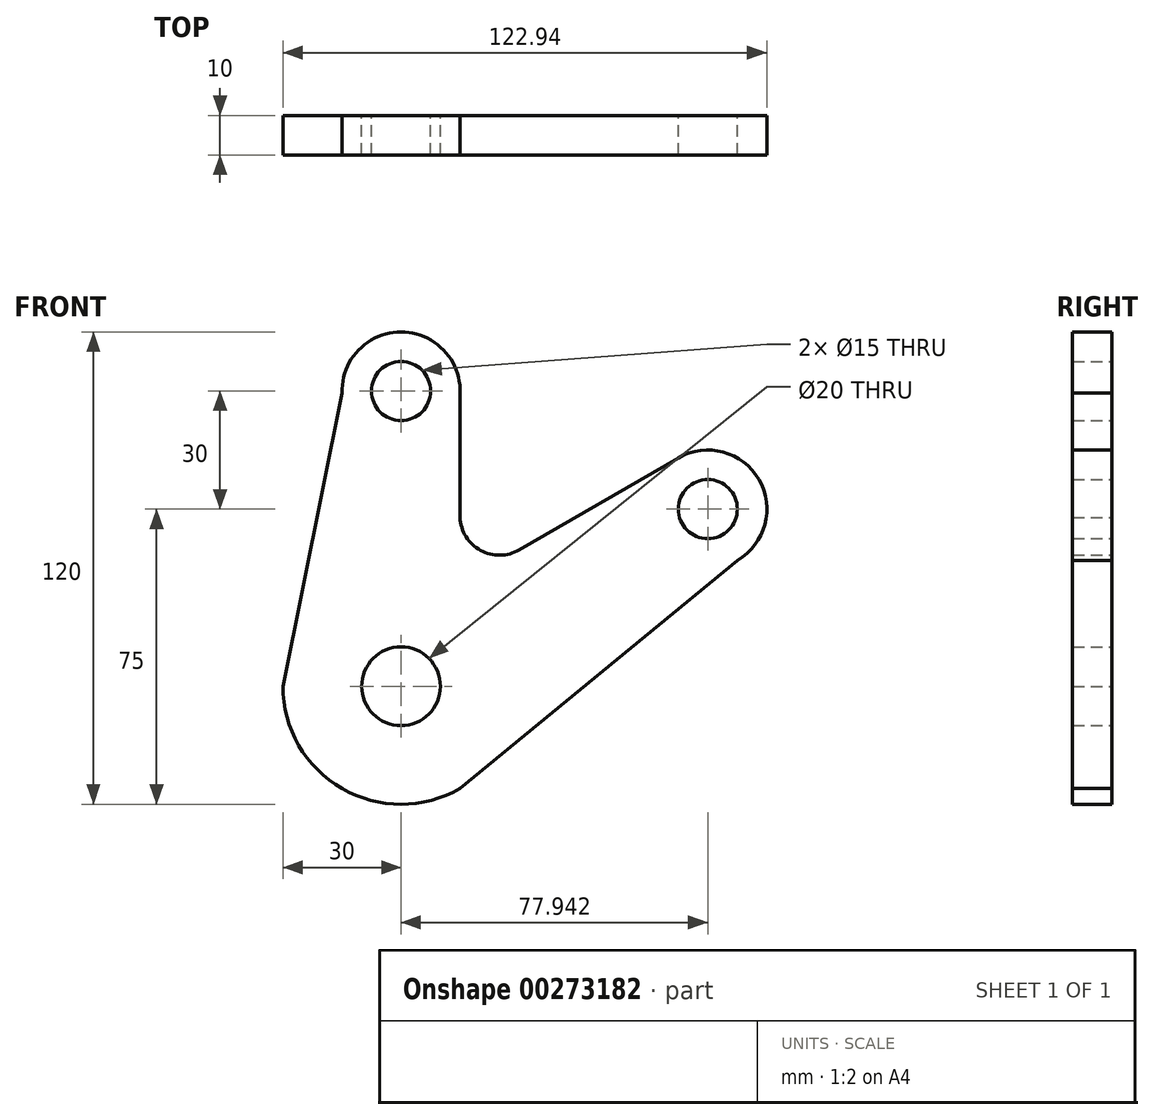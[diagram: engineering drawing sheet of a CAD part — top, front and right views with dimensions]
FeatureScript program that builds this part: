
annotation { "Feature Type Name" : "Feature", "Feature Type Description" : "" }
export const myFeature = defineFeature(function(context is Context, id is Id, definition is map)
    precondition{}
    {
        {
            var Q0;
            Q0=qCreatedBy(makeId("Front.planeOp"),FACE);
            var sketch = newSketch(context, id + "F0", { "sketchPlane" : qUnion([Q0])});
            skCircle(sketch, "E0", {"center": v(0, 0) * mm, "radius": 10 * mm});
            skCircle(sketch, "E1", {"center": v(0, 75) * mm, "radius": 7.5 * mm});
            skCircle(sketch, "E2", {"center": v(77.94, 45) * mm, "radius": 7.5 * mm});
            skLineSegment(sketch, "E3", {"start": v(0, 0) * mm, "end": v(77.94, 45) * mm, "construction": true});
            skArc(sketch, "E4", {"start": v(15, 74.5) * mm, "mid": v(0, 90) * mm, "end": v(-15, 74.5) * mm});
            skArc(sketch, "E5", {"start": v(85.44, 32) * mm, "mid": v(90.93, 52.5) * mm, "end": v(70.44, 58) * mm});
            skPoint(sketch, "E6.visualSharp", {"position": v(15, 25.98) * mm});
            skArc(sketch, "E7", {"start": v(-30, 0) * mm, "mid": v(-15, -25.98) * mm, "end": v(15, -25.99) * mm});
            skLineSegment(sketch, "E8", {"start": v(-30, 0) * mm, "end": v(-15, 74.5) * mm});
            skLineSegment(sketch, "E9", {"start": v(15, -25.99) * mm, "end": v(85.44, 32) * mm});
            skLineSegment(sketch, "E10", {"start": v(70.44, 58) * mm, "end": v(30, 34.64) * mm});
            skLineSegment(sketch, "E11", {"start": v(15, 74.5) * mm, "end": v(15, 42.83) * mm});
            skArc(sketch, "E12", {"start": v(15, 42.83) * mm, "mid": v(20.2, 34.51) * mm, "end": v(30, 34.64) * mm});
            skSolve(sketch);
        }
        {
            var Q0;
            Q0=makeQuery(id+"F0.imprint","IMPRINT",FACE,{"disambiguationData":[TD([[makeQuery(id+"F0.imprint","IMPRINT",EDGE,{"derivedFrom":sQuery(id+"F0.wireOp",EDGE,"E0")}),-1.0]])]});
            extrude(context, id + "F1", {"entities" : qUnion([Q0]), "depth" : 10 * mm});
        }
    });
